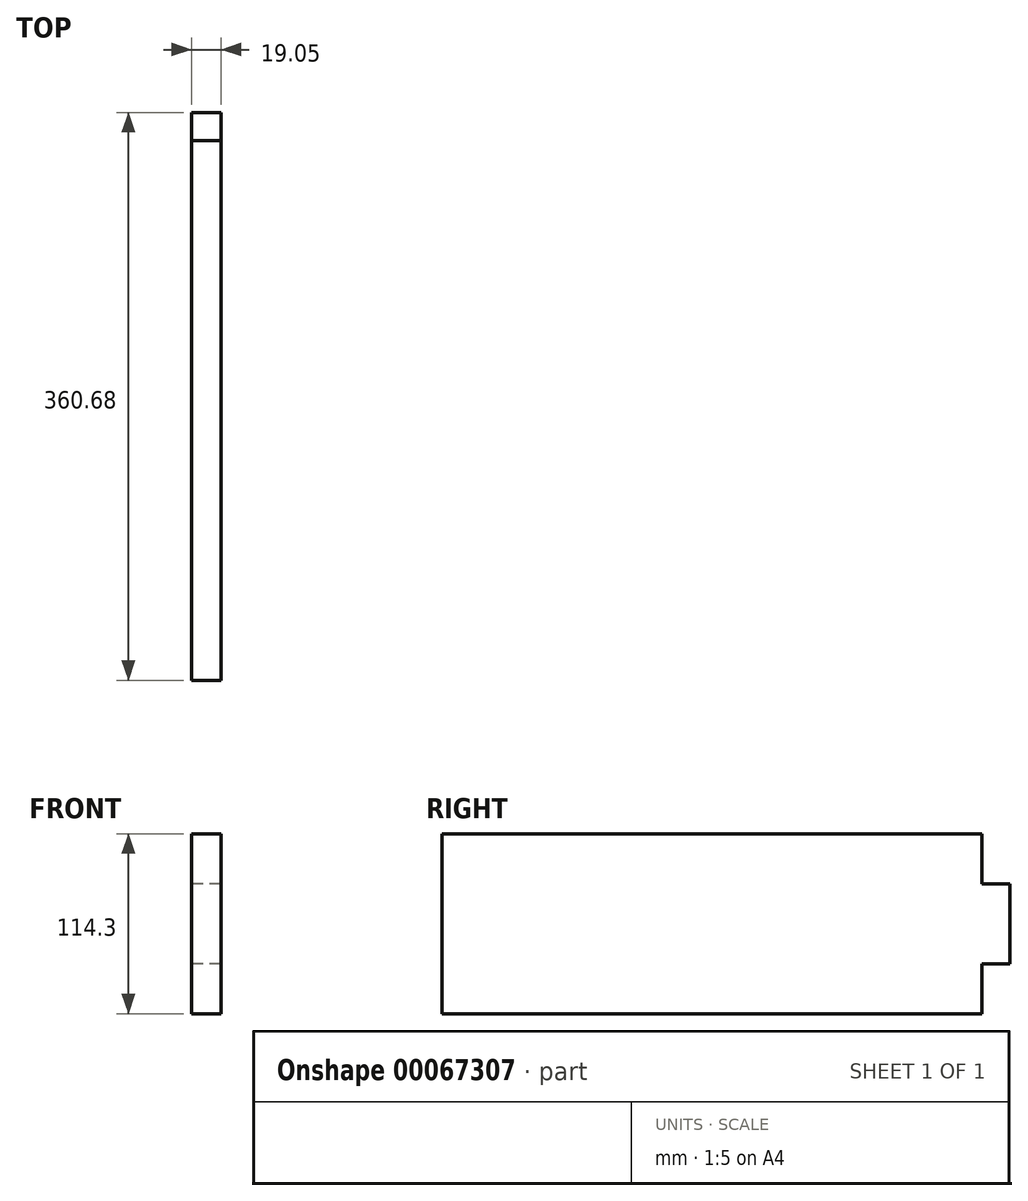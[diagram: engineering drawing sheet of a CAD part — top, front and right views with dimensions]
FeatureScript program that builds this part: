
annotation { "Feature Type Name" : "Feature", "Feature Type Description" : "" }
export const myFeature = defineFeature(function(context is Context, id is Id, definition is map)
    precondition{}
    {
        {
            var Q0;
            Q0=qCreatedBy(makeId("Right.planeOp"),FACE);
            var sketch = newSketch(context, id + "F0", { "sketchPlane" : qUnion([Q0])});
            skLineSegment(sketch, "E0.bottom", {"start": v(-171.45, 0) * mm, "end": v(171.45, 0) * mm});
            skLineSegment(sketch, "E0.top", {"start": v(-171.45, -114.3) * mm, "end": v(171.45, -114.3) * mm});
            skLineSegment(sketch, "E0.left", {"start": v(-171.45, 0) * mm, "end": v(-171.45, -114.3) * mm});
            skLineSegment(sketch, "E0.right", {"start": v(171.45, 0) * mm, "end": v(171.45, -114.3) * mm});
            skLineSegment(sketch, "E1.bottom", {"start": v(-69.85, -114.3) * mm, "end": v(82.55, -114.3) * mm});
            skLineSegment(sketch, "E1.top", {"start": v(-69.85, -132.08) * mm, "end": v(82.55, -132.08) * mm});
            skLineSegment(sketch, "E1.left", {"start": v(-69.85, -114.3) * mm, "end": v(-69.85, -132.08) * mm});
            skLineSegment(sketch, "E1.right", {"start": v(82.55, -114.3) * mm, "end": v(82.55, -132.08) * mm});
            skLineSegment(sketch, "E2.bottom", {"start": v(171.45, -31.75) * mm, "end": v(189.23, -31.75) * mm});
            skLineSegment(sketch, "E2.top", {"start": v(171.45, -82.55) * mm, "end": v(189.23, -82.55) * mm});
            skLineSegment(sketch, "E2.left", {"start": v(171.45, -31.75) * mm, "end": v(171.45, -82.55) * mm});
            skLineSegment(sketch, "E2.right", {"start": v(189.23, -31.75) * mm, "end": v(189.23, -82.55) * mm});
            skLineSegment(sketch, "E3", {"start": v(82.55, -114.3) * mm, "end": v(171.45, -114.3) * mm});
            skLineSegment(sketch, "E4.bottom", {"start": v(-69.85, 0) * mm, "end": v(82.55, 0) * mm});
            skLineSegment(sketch, "E4.top", {"start": v(-69.85, 17.78) * mm, "end": v(82.55, 17.78) * mm});
            skLineSegment(sketch, "E4.left", {"start": v(-69.85, 0) * mm, "end": v(-69.85, 17.78) * mm});
            skLineSegment(sketch, "E4.right", {"start": v(82.55, 0) * mm, "end": v(82.55, 17.78) * mm});
            skSolve(sketch);
        }
        {
            var Q0;
            {var subQ4=sQuery(id+"F0.wireOp",EDGE,"E0.left");Q0=makeQuery(id+"F0.imprint","IMPRINT",FACE,{"disambiguationData":[TD([[makeQuery(id+"F0.imprint","IMPRINT",EDGE,{"derivedFrom":subQ4}),1.0]])]});}
            var Q1;
            Q1=makeQuery(id+"F0.imprint","IMPRINT",FACE,{"disambiguationData":[TD([[makeQuery(id+"F0.imprint","IMPRINT",EDGE,{"derivedFrom":sQuery(id+"F0.wireOp",EDGE,"2062a582-d9c8-4e96-ad8d-9322998dc825.bottom")}),1.0]])]});
            var Q2;
            Q2=makeQuery(id+"F0.imprint","IMPRINT",FACE,{"disambiguationData":[TD([[makeQuery(id+"F0.imprint","IMPRINT",EDGE,{"derivedFrom":sQuery(id+"F0.wireOp",EDGE,"E1.bottom")}),-1.0]])]});
            var Q3;
            Q3=makeQuery(id+"F0.imprint","IMPRINT",FACE,{"disambiguationData":[TD([[makeQuery(id+"F0.imprint","IMPRINT",EDGE,{"derivedFrom":sQuery(id+"F0.wireOp",EDGE,"E2.bottom")}),-1.0]])]});
            var Q4;
            Q4=makeQuery(id+"F0.imprint","IMPRINT",FACE,{"disambiguationData":[TD([[makeQuery(id+"F0.imprint","IMPRINT",EDGE,{"derivedFrom":sQuery(id+"F0.wireOp",EDGE,"E4.bottom")}),1.0]])]});
            extrude(context, id + "F1", {"entities" : qUnion([Q0, Q1, Q2, Q3, Q4]), "depth" : 19.05 * mm});
        }
    });
